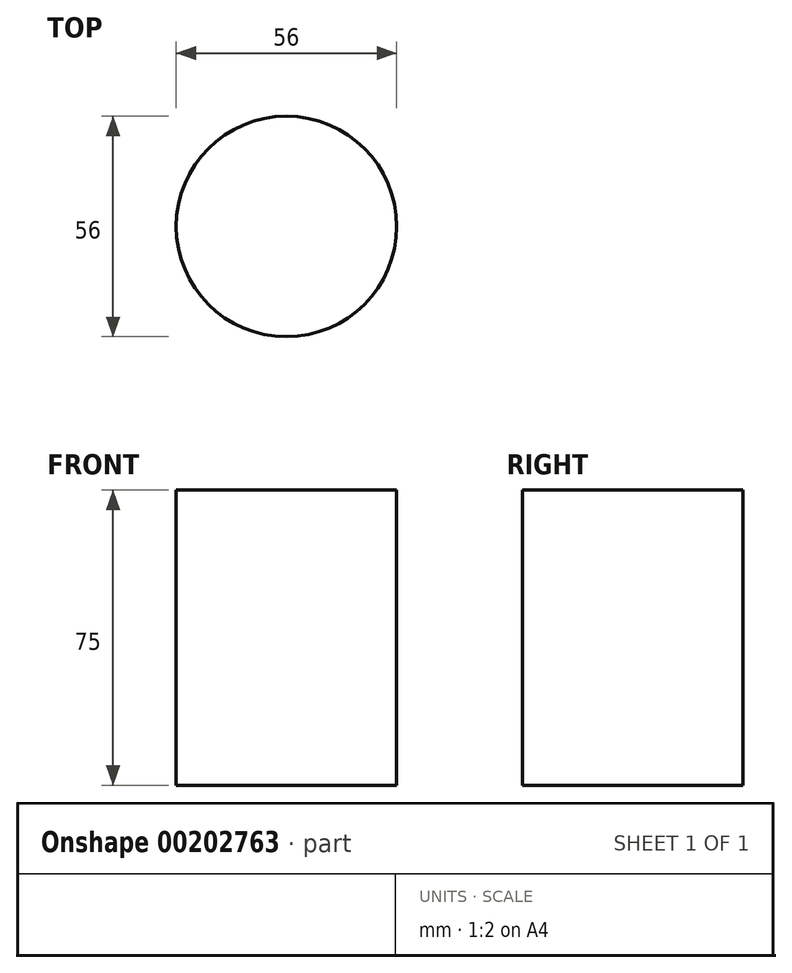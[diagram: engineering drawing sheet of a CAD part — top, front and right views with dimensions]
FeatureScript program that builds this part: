
annotation { "Feature Type Name" : "Feature", "Feature Type Description" : "" }
export const myFeature = defineFeature(function(context is Context, id is Id, definition is map)
    precondition{}
    {
        {
            var Q0;
            Q0=qCreatedBy(makeId("Top.planeOp"),FACE);
            var sketch = newSketch(context, id + "F0", { "sketchPlane" : qUnion([Q0])});
            skCircle(sketch, "E0.0", {"center": v(0, 0) * mm, "radius": 28 * mm});
            skSolve(sketch);
        }
        {
            var Q0;
            Q0 = qSketchRegion(id + "F0", true);
            extrude(context, id + "F1", {"entities" : qUnion([Q0]), "depth" : 75 * mm});
        }
    });
